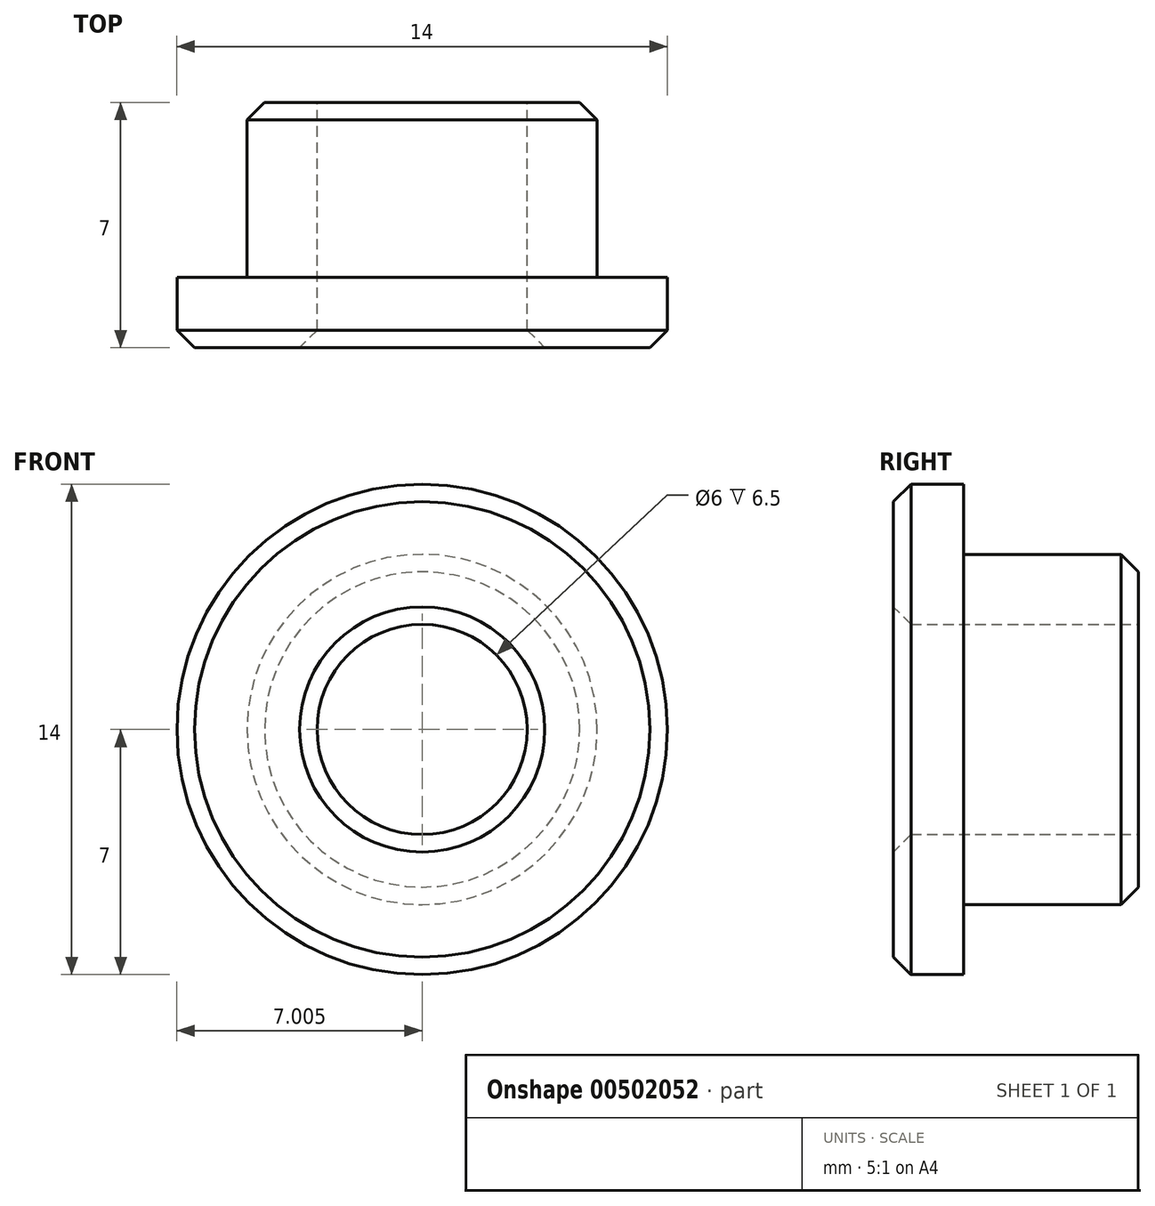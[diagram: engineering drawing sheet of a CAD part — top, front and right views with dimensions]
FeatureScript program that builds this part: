
annotation { "Feature Type Name" : "Feature", "Feature Type Description" : "" }
export const myFeature = defineFeature(function(context is Context, id is Id, definition is map)
    precondition{}
    {
        {
            var Q0;
            Q0=qCreatedBy(makeId("Front.planeOp"),FACE);
            var sketch = newSketch(context, id + "F0", { "sketchPlane" : qUnion([Q0])});
            skCircle(sketch, "E0", {"center": v(1.21, 0) * mm, "radius": 5 * mm});
            skCircle(sketch, "E1", {"center": v(1.21, 0) * mm, "radius": 3 * mm});
            skSolve(sketch);
        }
        {
            var Q0;
            Q0 = qSketchRegion(id + "F0", true);
            extrude(context, id + "F1", {"entities" : qUnion([Q0]), "depth" : 5 * mm});
        }
        {
            var Q0;
            Q0=makeQuery(id+"F1.opExtrude","CAP_FACE",FACE,{"disambiguationData":[OSD([sQuery(id+"F0.wireOp",EDGE,"E0"),sQuery(id+"F0.wireOp",EDGE,"E1")])],"isStart":false});
            var sketch = newSketch(context, id + "F2", { "sketchPlane" : qUnion([Q0])});
            skCircle(sketch, "E2.0", {"center": v(1.21, 0) * mm, "radius": 7 * mm});
            skSolve(sketch);
        }
        {
            var Q0;
            Q0=makeQuery(id+"F2.imprint","IMPRINT",FACE,{"disambiguationData":[TD([[makeQuery(id+"F2.imprint","IMPRINT",EDGE,{"derivedFrom":sQuery(id+"F2.wireOp",EDGE,"E2.0")}),1.0]])]});
            var Q1;
            Q1=makeQuery(id+"F2.imprint","IMPRINT",FACE,{"disambiguationData":[TD([[makeQuery(id+"F2.imprint","IMPRINT",EDGE,{"derivedFrom":makeQuery(id+"F1.opExtrude","CAP_EDGE",EDGE,{"disambiguationData":[OSD([sQuery(id+"F0.wireOp",EDGE,"E0")])],"isStart":false})}),1.0]])]});
            extrude(context, id + "F3", {"entities" : qUnion([Q0, Q1]), "operationType" : NewBodyOperationType.ADD, "depth" : 2 * mm});
        }
        {
            var Q0;
            Q0=makeQuery(id+"F3.opExtrude","CAP_EDGE",EDGE,{"disambiguationData":[OSD([sQuery(id+"F0.wireOp",EDGE,"E1")])],"isStart":false});
            chamfer(context, id + "F4", {"entities" : qUnion([Q0]), "width" : 0.5 * mm, "tangentPropagation" : true});
        }
        {
            var Q0;
            Q0=makeQuery(id+"F3.opExtrude","CAP_EDGE",EDGE,{"disambiguationData":[OSD([sQuery(id+"F2.wireOp",EDGE,"E2.0")])],"isStart":false});
            chamfer(context, id + "F5", {"entities" : qUnion([Q0]), "width" : 0.5 * mm, "tangentPropagation" : true});
        }
        {
            var Q0;
            Q0=makeQuery(id+"F1.opExtrude","CAP_EDGE",EDGE,{"disambiguationData":[OSD([sQuery(id+"F0.wireOp",EDGE,"E0")])],"isStart":true});
            chamfer(context, id + "F6", {"entities" : qUnion([Q0]), "width" : 0.5 * mm, "tangentPropagation" : true});
        }
    });
